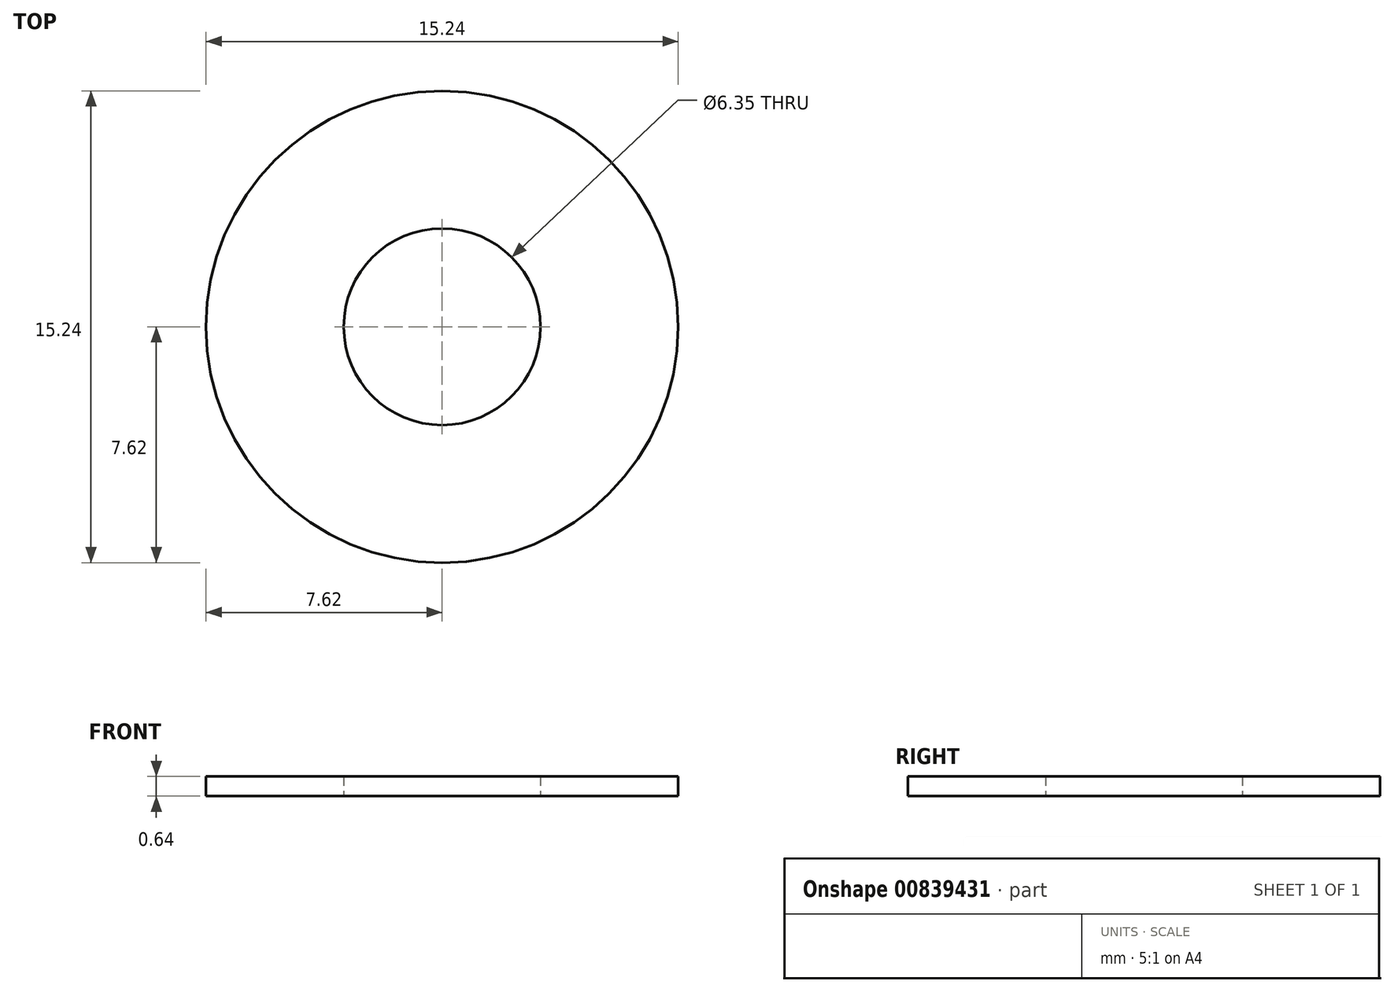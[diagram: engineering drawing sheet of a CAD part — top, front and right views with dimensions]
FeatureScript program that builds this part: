
annotation { "Feature Type Name" : "Feature", "Feature Type Description" : "" }
export const myFeature = defineFeature(function(context is Context, id is Id, definition is map)
    precondition{}
    {
        {
            var Q0;
            Q0=qCreatedBy(makeId("Top.planeOp"),FACE);
            var sketch = newSketch(context, id + "F0", { "sketchPlane" : qUnion([Q0])});
            skCircle(sketch, "E0", {"center": v(0, 0) * mm, "radius": 3.18 * mm});
            skCircle(sketch, "E1", {"center": v(0, 0) * mm, "radius": 7.62 * mm});
            skSolve(sketch);
        }
        {
            var Q0;
            Q0 = qSketchRegion(id + "F0", true);
            extrude(context, id + "F1", {"entities" : qUnion([Q0]), "depth" : 0.64 * mm, "offsetDistance" : 25.4 * mm});
        }
    });
